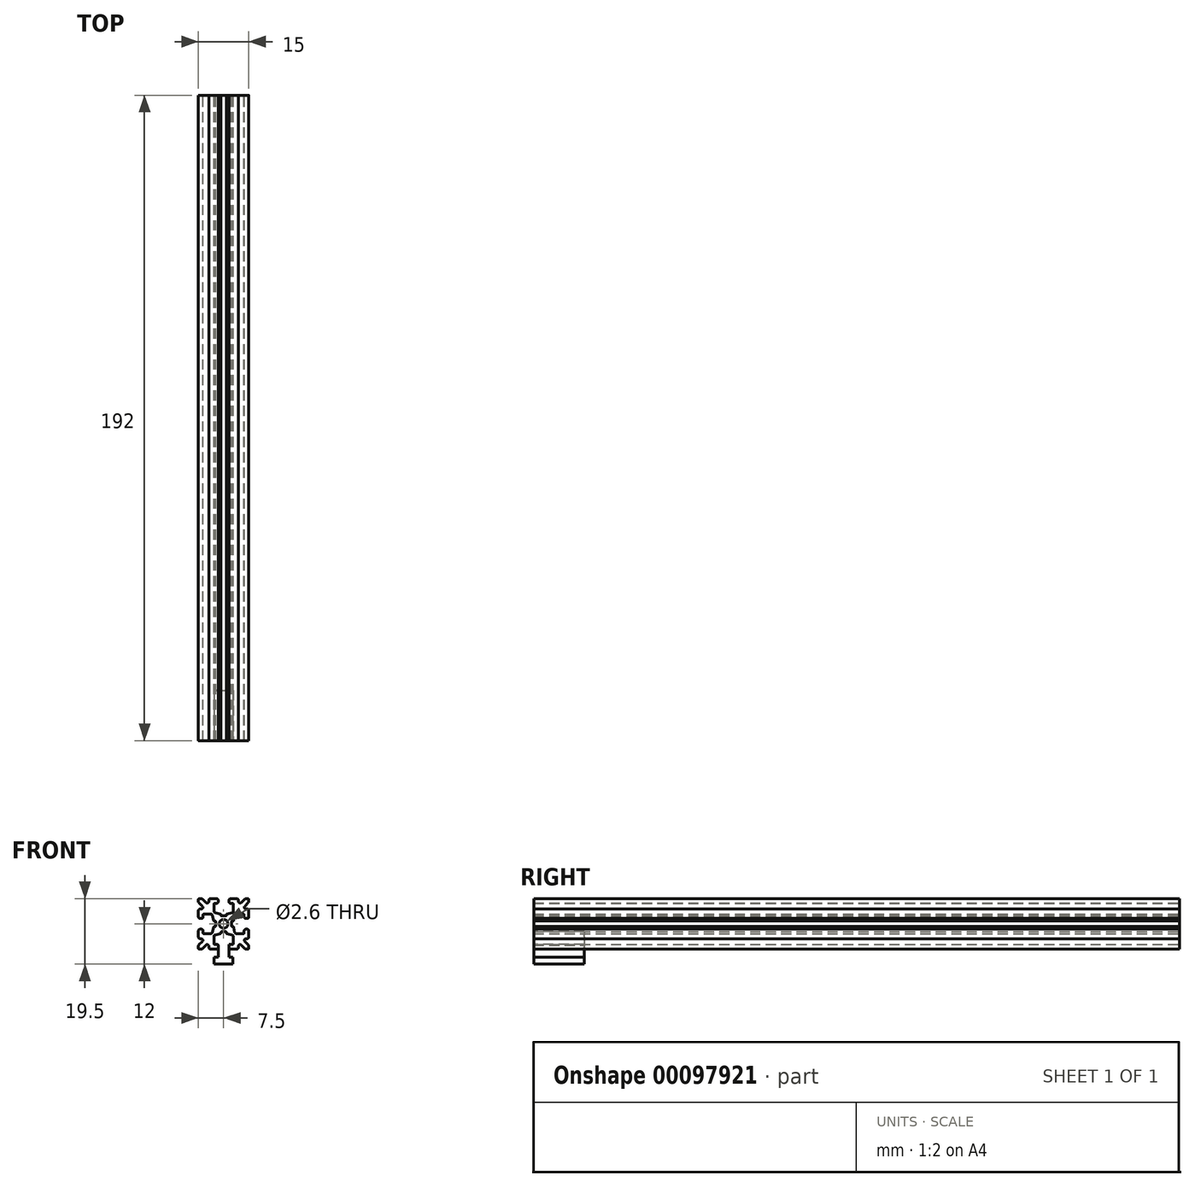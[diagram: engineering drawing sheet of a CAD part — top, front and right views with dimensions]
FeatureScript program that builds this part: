
annotation { "Feature Type Name" : "Feature", "Feature Type Description" : "" }
export const myFeature = defineFeature(function(context is Context, id is Id, definition is map)
    precondition{}
    {
        {
            var Q0;
            Q0=qCreatedBy(makeId("Front.planeOp"),FACE);
            var sketch = newSketch(context, id + "F0", { "sketchPlane" : qUnion([Q0])});
            skLineSegment(sketch, "E0.0.0", {"start": v(0.83, -2.55) * mm, "end": v(0.83, -2.77) * mm});
            skArc(sketch, "E0.0.1", {"start": v(0.83, -2.77) * mm, "mid": v(0.87, -2.9) * mm, "end": v(0.98, -2.97) * mm});
            skLineSegment(sketch, "E0.0.2", {"start": v(0.98, -2.97) * mm, "end": v(2.5, -3.31) * mm});
            skArc(sketch, "E0.0.3", {"start": v(2.5, -3.31) * mm, "mid": v(2.8, -3.49) * mm, "end": v(2.9, -3.8) * mm});
            skLineSegment(sketch, "E0.0.4", {"start": v(2.9, -3.8) * mm, "end": v(2.9, -5.9) * mm});
            skArc(sketch, "E0.0.5", {"start": v(2.9, -5.9) * mm, "mid": v(2.84, -6.04) * mm, "end": v(2.7, -6.1) * mm});
            skLineSegment(sketch, "E0.0.6", {"start": v(2.7, -6.1) * mm, "end": v(2.1, -6.1) * mm});
            skArc(sketch, "E0.0.7", {"start": v(2.1, -6.1) * mm, "mid": v(1.75, -6.25) * mm, "end": v(1.6, -6.6) * mm});
            skLineSegment(sketch, "E0.0.8", {"start": v(1.6, -6.6) * mm, "end": v(1.6, -7) * mm});
            skArc(sketch, "E0.0.9", {"start": v(1.6, -7) * mm, "mid": v(1.75, -7.35) * mm, "end": v(2.1, -7.5) * mm});
            skLineSegment(sketch, "E0.0.10", {"start": v(2.1, -7.5) * mm, "end": v(3.9, -7.5) * mm});
            skArc(sketch, "E0.0.11", {"start": v(3.9, -7.5) * mm, "mid": v(4.25, -7.35) * mm, "end": v(4.4, -7) * mm});
            skLineSegment(sketch, "E0.0.12", {"start": v(4.4, -7) * mm, "end": v(4.4, -6.67) * mm});
            skArc(sketch, "E0.0.13", {"start": v(4.4, -6.67) * mm, "mid": v(4.7, -6.2) * mm, "end": v(5.25, -6.31) * mm});
            skLineSegment(sketch, "E0.0.14", {"start": v(5.25, -6.31) * mm, "end": v(6.3, -7.35) * mm});
            skArc(sketch, "E0.0.15", {"start": v(6.3, -7.35) * mm, "mid": v(6.46, -7.46) * mm, "end": v(6.65, -7.5) * mm});
            skLineSegment(sketch, "E0.0.16", {"start": v(6.65, -7.5) * mm, "end": v(7.25, -7.5) * mm});
            skArc(sketch, "E0.0.17", {"start": v(7.25, -7.5) * mm, "mid": v(7.43, -7.43) * mm, "end": v(7.5, -7.25) * mm});
            skLineSegment(sketch, "E0.0.18", {"start": v(7.5, -7.25) * mm, "end": v(7.5, -6.65) * mm});
            skArc(sketch, "E0.0.19", {"start": v(7.5, -6.65) * mm, "mid": v(7.46, -6.46) * mm, "end": v(7.35, -6.3) * mm});
            skLineSegment(sketch, "E0.0.20", {"start": v(7.35, -6.3) * mm, "end": v(6.31, -5.25) * mm});
            skArc(sketch, "E0.0.21", {"start": v(6.31, -5.25) * mm, "mid": v(6.2, -4.7) * mm, "end": v(6.67, -4.4) * mm});
            skLineSegment(sketch, "E0.0.22", {"start": v(6.67, -4.4) * mm, "end": v(7, -4.4) * mm});
            skArc(sketch, "E0.0.23", {"start": v(7, -4.4) * mm, "mid": v(7.35, -4.25) * mm, "end": v(7.5, -3.9) * mm});
            skLineSegment(sketch, "E0.0.24", {"start": v(7.5, -3.9) * mm, "end": v(7.5, -2.1) * mm});
            skArc(sketch, "E0.0.25", {"start": v(7.5, -2.1) * mm, "mid": v(7.35, -1.75) * mm, "end": v(7, -1.6) * mm});
            skLineSegment(sketch, "E0.0.26", {"start": v(7, -1.6) * mm, "end": v(6.6, -1.6) * mm});
            skArc(sketch, "E0.0.27", {"start": v(6.6, -1.6) * mm, "mid": v(6.25, -1.75) * mm, "end": v(6.1, -2.1) * mm});
            skLineSegment(sketch, "E0.0.28", {"start": v(6.1, -2.1) * mm, "end": v(6.1, -2.7) * mm});
            skArc(sketch, "E0.0.29", {"start": v(6.1, -2.7) * mm, "mid": v(6.04, -2.84) * mm, "end": v(5.9, -2.9) * mm});
            skLineSegment(sketch, "E0.0.30", {"start": v(5.9, -2.9) * mm, "end": v(3.8, -2.9) * mm});
            skArc(sketch, "E0.0.31", {"start": v(3.8, -2.9) * mm, "mid": v(3.49, -2.8) * mm, "end": v(3.31, -2.5) * mm});
            skLineSegment(sketch, "E0.0.32", {"start": v(3.31, -2.5) * mm, "end": v(2.97, -0.98) * mm});
            skArc(sketch, "E0.0.33", {"start": v(2.97, -0.98) * mm, "mid": v(2.9, -0.87) * mm, "end": v(2.77, -0.83) * mm});
            skLineSegment(sketch, "E0.0.34", {"start": v(2.77, -0.83) * mm, "end": v(2.55, -0.83) * mm});
            skArc(sketch, "E0.0.35", {"start": v(2.55, -0.83) * mm, "mid": v(2.4, -0.77) * mm, "end": v(2.35, -0.63) * mm});
            skLineSegment(sketch, "E0.0.36", {"start": v(2.35, -0.63) * mm, "end": v(2.35, 0.63) * mm});
            skArc(sketch, "E0.0.37", {"start": v(2.35, 0.63) * mm, "mid": v(2.4, 0.77) * mm, "end": v(2.55, 0.83) * mm});
            skLineSegment(sketch, "E0.0.38", {"start": v(2.55, 0.83) * mm, "end": v(2.77, 0.83) * mm});
            skArc(sketch, "E0.0.39", {"start": v(2.77, 0.83) * mm, "mid": v(2.9, 0.87) * mm, "end": v(2.97, 0.98) * mm});
            skLineSegment(sketch, "E0.0.40", {"start": v(2.97, 0.98) * mm, "end": v(3.31, 2.5) * mm});
            skArc(sketch, "E0.0.41", {"start": v(3.31, 2.5) * mm, "mid": v(3.49, 2.8) * mm, "end": v(3.8, 2.9) * mm});
            skLineSegment(sketch, "E0.0.42", {"start": v(3.8, 2.9) * mm, "end": v(5.9, 2.9) * mm});
            skArc(sketch, "E0.0.43", {"start": v(5.9, 2.9) * mm, "mid": v(6.04, 2.84) * mm, "end": v(6.1, 2.7) * mm});
            skLineSegment(sketch, "E0.0.44", {"start": v(6.1, 2.7) * mm, "end": v(6.1, 2.1) * mm});
            skArc(sketch, "E0.0.45", {"start": v(6.1, 2.1) * mm, "mid": v(6.25, 1.75) * mm, "end": v(6.6, 1.6) * mm});
            skLineSegment(sketch, "E0.0.46", {"start": v(6.6, 1.6) * mm, "end": v(7, 1.6) * mm});
            skArc(sketch, "E0.0.47", {"start": v(7, 1.6) * mm, "mid": v(7.35, 1.75) * mm, "end": v(7.5, 2.1) * mm});
            skLineSegment(sketch, "E0.0.48", {"start": v(7.5, 2.1) * mm, "end": v(7.5, 3.9) * mm});
            skArc(sketch, "E0.0.49", {"start": v(7.5, 3.9) * mm, "mid": v(7.35, 4.25) * mm, "end": v(7, 4.4) * mm});
            skLineSegment(sketch, "E0.0.50", {"start": v(7, 4.4) * mm, "end": v(6.67, 4.4) * mm});
            skArc(sketch, "E0.0.51", {"start": v(6.67, 4.4) * mm, "mid": v(6.2, 4.7) * mm, "end": v(6.31, 5.25) * mm});
            skLineSegment(sketch, "E0.0.52", {"start": v(6.31, 5.25) * mm, "end": v(7.35, 6.3) * mm});
            skArc(sketch, "E0.0.53", {"start": v(7.35, 6.3) * mm, "mid": v(7.46, 6.46) * mm, "end": v(7.5, 6.65) * mm});
            skLineSegment(sketch, "E0.0.54", {"start": v(7.5, 6.65) * mm, "end": v(7.5, 7.25) * mm});
            skArc(sketch, "E0.0.55", {"start": v(7.5, 7.25) * mm, "mid": v(7.43, 7.43) * mm, "end": v(7.25, 7.5) * mm});
            skLineSegment(sketch, "E0.0.56", {"start": v(7.25, 7.5) * mm, "end": v(6.65, 7.5) * mm});
            skArc(sketch, "E0.0.57", {"start": v(6.65, 7.5) * mm, "mid": v(6.46, 7.46) * mm, "end": v(6.3, 7.35) * mm});
            skLineSegment(sketch, "E0.0.58", {"start": v(6.3, 7.35) * mm, "end": v(5.25, 6.31) * mm});
            skArc(sketch, "E0.0.59", {"start": v(5.25, 6.31) * mm, "mid": v(4.7, 6.2) * mm, "end": v(4.4, 6.67) * mm});
            skLineSegment(sketch, "E0.0.60", {"start": v(4.4, 6.67) * mm, "end": v(4.4, 7) * mm});
            skArc(sketch, "E0.0.61", {"start": v(4.4, 7) * mm, "mid": v(4.25, 7.35) * mm, "end": v(3.9, 7.5) * mm});
            skLineSegment(sketch, "E0.0.62", {"start": v(3.9, 7.5) * mm, "end": v(2.1, 7.5) * mm});
            skArc(sketch, "E0.0.63", {"start": v(2.1, 7.5) * mm, "mid": v(1.75, 7.35) * mm, "end": v(1.6, 7) * mm});
            skLineSegment(sketch, "E0.0.64", {"start": v(1.6, 7) * mm, "end": v(1.6, 6.6) * mm});
            skArc(sketch, "E0.0.65", {"start": v(1.6, 6.6) * mm, "mid": v(1.75, 6.25) * mm, "end": v(2.1, 6.1) * mm});
            skLineSegment(sketch, "E0.0.66", {"start": v(2.1, 6.1) * mm, "end": v(2.7, 6.1) * mm});
            skArc(sketch, "E0.0.67", {"start": v(2.7, 6.1) * mm, "mid": v(2.84, 6.04) * mm, "end": v(2.9, 5.9) * mm});
            skLineSegment(sketch, "E0.0.68", {"start": v(2.9, 5.9) * mm, "end": v(2.9, 3.8) * mm});
            skArc(sketch, "E0.0.69", {"start": v(2.9, 3.8) * mm, "mid": v(2.8, 3.49) * mm, "end": v(2.5, 3.31) * mm});
            skLineSegment(sketch, "E0.0.70", {"start": v(2.5, 3.31) * mm, "end": v(0.98, 2.97) * mm});
            skArc(sketch, "E0.0.71", {"start": v(0.98, 2.97) * mm, "mid": v(0.87, 2.9) * mm, "end": v(0.83, 2.77) * mm});
            skLineSegment(sketch, "E0.0.72", {"start": v(0.83, 2.77) * mm, "end": v(0.83, 2.55) * mm});
            skArc(sketch, "E0.0.73", {"start": v(0.83, 2.55) * mm, "mid": v(0.77, 2.4) * mm, "end": v(0.63, 2.35) * mm});
            skLineSegment(sketch, "E0.0.74", {"start": v(0.63, 2.35) * mm, "end": v(-0.63, 2.35) * mm});
            skArc(sketch, "E0.0.75", {"start": v(-0.63, 2.35) * mm, "mid": v(-0.77, 2.4) * mm, "end": v(-0.83, 2.55) * mm});
            skLineSegment(sketch, "E0.0.76", {"start": v(-0.83, 2.55) * mm, "end": v(-0.83, 2.77) * mm});
            skArc(sketch, "E0.0.77", {"start": v(-0.83, 2.77) * mm, "mid": v(-0.87, 2.9) * mm, "end": v(-0.98, 2.97) * mm});
            skLineSegment(sketch, "E0.0.78", {"start": v(-0.98, 2.97) * mm, "end": v(-2.5, 3.31) * mm});
            skArc(sketch, "E0.0.79", {"start": v(-2.5, 3.31) * mm, "mid": v(-2.8, 3.49) * mm, "end": v(-2.9, 3.8) * mm});
            skLineSegment(sketch, "E0.0.80", {"start": v(-2.9, 3.8) * mm, "end": v(-2.9, 5.9) * mm});
            skArc(sketch, "E0.0.81", {"start": v(-2.9, 5.9) * mm, "mid": v(-2.84, 6.04) * mm, "end": v(-2.7, 6.1) * mm});
            skLineSegment(sketch, "E0.0.82", {"start": v(-2.7, 6.1) * mm, "end": v(-2.1, 6.1) * mm});
            skArc(sketch, "E0.0.83", {"start": v(-2.1, 6.1) * mm, "mid": v(-1.75, 6.25) * mm, "end": v(-1.6, 6.6) * mm});
            skLineSegment(sketch, "E0.0.84", {"start": v(-1.6, 6.6) * mm, "end": v(-1.6, 7) * mm});
            skArc(sketch, "E0.0.85", {"start": v(-1.6, 7) * mm, "mid": v(-1.75, 7.35) * mm, "end": v(-2.1, 7.5) * mm});
            skLineSegment(sketch, "E0.0.86", {"start": v(-2.1, 7.5) * mm, "end": v(-3.9, 7.5) * mm});
            skArc(sketch, "E0.0.87", {"start": v(-3.9, 7.5) * mm, "mid": v(-4.25, 7.35) * mm, "end": v(-4.4, 7) * mm});
            skLineSegment(sketch, "E0.0.88", {"start": v(-4.4, 7) * mm, "end": v(-4.4, 6.67) * mm});
            skArc(sketch, "E0.0.89", {"start": v(-4.4, 6.67) * mm, "mid": v(-4.7, 6.2) * mm, "end": v(-5.25, 6.31) * mm});
            skLineSegment(sketch, "E0.0.90", {"start": v(-5.25, 6.31) * mm, "end": v(-6.3, 7.35) * mm});
            skArc(sketch, "E0.0.91", {"start": v(-6.3, 7.35) * mm, "mid": v(-6.46, 7.46) * mm, "end": v(-6.65, 7.5) * mm});
            skLineSegment(sketch, "E0.0.92", {"start": v(-6.65, 7.5) * mm, "end": v(-7.25, 7.5) * mm});
            skArc(sketch, "E0.0.93", {"start": v(-7.25, 7.5) * mm, "mid": v(-7.43, 7.43) * mm, "end": v(-7.5, 7.25) * mm});
            skLineSegment(sketch, "E0.0.94", {"start": v(-7.5, 7.25) * mm, "end": v(-7.5, 6.65) * mm});
            skArc(sketch, "E0.0.95", {"start": v(-7.5, 6.65) * mm, "mid": v(-7.46, 6.46) * mm, "end": v(-7.35, 6.3) * mm});
            skLineSegment(sketch, "E0.0.96", {"start": v(-7.35, 6.3) * mm, "end": v(-6.31, 5.25) * mm});
            skArc(sketch, "E0.0.97", {"start": v(-6.31, 5.25) * mm, "mid": v(-6.2, 4.7) * mm, "end": v(-6.67, 4.4) * mm});
            skLineSegment(sketch, "E0.0.98", {"start": v(-6.67, 4.4) * mm, "end": v(-7, 4.4) * mm});
            skArc(sketch, "E0.0.99", {"start": v(-7, 4.4) * mm, "mid": v(-7.35, 4.25) * mm, "end": v(-7.5, 3.9) * mm});
            skLineSegment(sketch, "E0.0.100", {"start": v(-7.5, 3.9) * mm, "end": v(-7.5, 2.1) * mm});
            skArc(sketch, "E0.0.101", {"start": v(-7.5, 2.1) * mm, "mid": v(-7.35, 1.75) * mm, "end": v(-7, 1.6) * mm});
            skLineSegment(sketch, "E0.0.102", {"start": v(-7, 1.6) * mm, "end": v(-6.6, 1.6) * mm});
            skArc(sketch, "E0.0.103", {"start": v(-6.6, 1.6) * mm, "mid": v(-6.25, 1.75) * mm, "end": v(-6.1, 2.1) * mm});
            skLineSegment(sketch, "E0.0.104", {"start": v(-6.1, 2.1) * mm, "end": v(-6.1, 2.7) * mm});
            skArc(sketch, "E0.0.105", {"start": v(-6.1, 2.7) * mm, "mid": v(-6.04, 2.84) * mm, "end": v(-5.9, 2.9) * mm});
            skLineSegment(sketch, "E0.0.106", {"start": v(-5.9, 2.9) * mm, "end": v(-3.8, 2.9) * mm});
            skArc(sketch, "E0.0.107", {"start": v(-3.8, 2.9) * mm, "mid": v(-3.49, 2.8) * mm, "end": v(-3.31, 2.5) * mm});
            skLineSegment(sketch, "E0.0.108", {"start": v(-3.31, 2.5) * mm, "end": v(-2.97, 0.98) * mm});
            skArc(sketch, "E0.0.109", {"start": v(-2.97, 0.98) * mm, "mid": v(-2.9, 0.87) * mm, "end": v(-2.77, 0.83) * mm});
            skLineSegment(sketch, "E0.0.110", {"start": v(-2.77, 0.83) * mm, "end": v(-2.55, 0.83) * mm});
            skArc(sketch, "E0.0.111", {"start": v(-2.55, 0.83) * mm, "mid": v(-2.4, 0.77) * mm, "end": v(-2.35, 0.63) * mm});
            skLineSegment(sketch, "E0.0.112", {"start": v(-2.35, 0.63) * mm, "end": v(-2.35, -0.63) * mm});
            skArc(sketch, "E0.0.113", {"start": v(-2.35, -0.63) * mm, "mid": v(-2.4, -0.77) * mm, "end": v(-2.55, -0.83) * mm});
            skLineSegment(sketch, "E0.0.114", {"start": v(-2.55, -0.83) * mm, "end": v(-2.77, -0.83) * mm});
            skArc(sketch, "E0.0.115", {"start": v(-2.77, -0.83) * mm, "mid": v(-2.9, -0.87) * mm, "end": v(-2.97, -0.98) * mm});
            skLineSegment(sketch, "E0.0.116", {"start": v(-2.97, -0.98) * mm, "end": v(-3.31, -2.5) * mm});
            skArc(sketch, "E0.0.117", {"start": v(-3.31, -2.5) * mm, "mid": v(-3.49, -2.8) * mm, "end": v(-3.8, -2.9) * mm});
            skLineSegment(sketch, "E0.0.118", {"start": v(-3.8, -2.9) * mm, "end": v(-5.9, -2.9) * mm});
            skArc(sketch, "E0.0.119", {"start": v(-5.9, -2.9) * mm, "mid": v(-6.04, -2.84) * mm, "end": v(-6.1, -2.7) * mm});
            skLineSegment(sketch, "E0.0.120", {"start": v(-6.1, -2.7) * mm, "end": v(-6.1, -2.1) * mm});
            skArc(sketch, "E0.0.121", {"start": v(-6.1, -2.1) * mm, "mid": v(-6.25, -1.75) * mm, "end": v(-6.6, -1.6) * mm});
            skLineSegment(sketch, "E0.0.122", {"start": v(-6.6, -1.6) * mm, "end": v(-7, -1.6) * mm});
            skArc(sketch, "E0.0.123", {"start": v(-7, -1.6) * mm, "mid": v(-7.35, -1.75) * mm, "end": v(-7.5, -2.1) * mm});
            skLineSegment(sketch, "E0.0.124", {"start": v(-7.5, -2.1) * mm, "end": v(-7.5, -3.9) * mm});
            skArc(sketch, "E0.0.125", {"start": v(-7.5, -3.9) * mm, "mid": v(-7.35, -4.25) * mm, "end": v(-7, -4.4) * mm});
            skLineSegment(sketch, "E0.0.126", {"start": v(-7, -4.4) * mm, "end": v(-6.67, -4.4) * mm});
            skArc(sketch, "E0.0.127", {"start": v(-6.67, -4.4) * mm, "mid": v(-6.2, -4.7) * mm, "end": v(-6.31, -5.25) * mm});
            skLineSegment(sketch, "E0.0.128", {"start": v(-6.31, -5.25) * mm, "end": v(-7.35, -6.3) * mm});
            skArc(sketch, "E0.0.129", {"start": v(-7.35, -6.3) * mm, "mid": v(-7.46, -6.46) * mm, "end": v(-7.5, -6.65) * mm});
            skLineSegment(sketch, "E0.0.130", {"start": v(-7.5, -6.65) * mm, "end": v(-7.5, -7.25) * mm});
            skArc(sketch, "E0.0.131", {"start": v(-7.5, -7.25) * mm, "mid": v(-7.43, -7.43) * mm, "end": v(-7.25, -7.5) * mm});
            skLineSegment(sketch, "E0.0.132", {"start": v(-7.25, -7.5) * mm, "end": v(-6.65, -7.5) * mm});
            skArc(sketch, "E0.0.133", {"start": v(-6.65, -7.5) * mm, "mid": v(-6.46, -7.46) * mm, "end": v(-6.3, -7.35) * mm});
            skLineSegment(sketch, "E0.0.134", {"start": v(-6.3, -7.35) * mm, "end": v(-5.25, -6.31) * mm});
            skArc(sketch, "E0.0.135", {"start": v(-5.25, -6.31) * mm, "mid": v(-4.7, -6.2) * mm, "end": v(-4.4, -6.67) * mm});
            skLineSegment(sketch, "E0.0.136", {"start": v(-4.4, -6.67) * mm, "end": v(-4.4, -7) * mm});
            skArc(sketch, "E0.0.137", {"start": v(-4.4, -7) * mm, "mid": v(-4.25, -7.35) * mm, "end": v(-3.9, -7.5) * mm});
            skLineSegment(sketch, "E0.0.138", {"start": v(-3.9, -7.5) * mm, "end": v(-2.1, -7.5) * mm});
            skArc(sketch, "E0.0.139", {"start": v(-2.1, -7.5) * mm, "mid": v(-1.75, -7.35) * mm, "end": v(-1.6, -7) * mm});
            skLineSegment(sketch, "E0.0.140", {"start": v(-1.6, -7) * mm, "end": v(-1.6, -6.6) * mm});
            skArc(sketch, "E0.0.141", {"start": v(-1.6, -6.6) * mm, "mid": v(-1.75, -6.25) * mm, "end": v(-2.1, -6.1) * mm});
            skLineSegment(sketch, "E0.0.142", {"start": v(-2.1, -6.1) * mm, "end": v(-2.7, -6.1) * mm});
            skArc(sketch, "E0.0.143", {"start": v(-2.7, -6.1) * mm, "mid": v(-2.84, -6.04) * mm, "end": v(-2.9, -5.9) * mm});
            skLineSegment(sketch, "E0.0.144", {"start": v(-2.9, -5.9) * mm, "end": v(-2.9, -3.8) * mm});
            skArc(sketch, "E0.0.145", {"start": v(-2.9, -3.8) * mm, "mid": v(-2.8, -3.49) * mm, "end": v(-2.5, -3.31) * mm});
            skLineSegment(sketch, "E0.0.146", {"start": v(-2.5, -3.31) * mm, "end": v(-0.98, -2.97) * mm});
            skArc(sketch, "E0.0.147", {"start": v(-0.98, -2.97) * mm, "mid": v(-0.87, -2.9) * mm, "end": v(-0.83, -2.77) * mm});
            skLineSegment(sketch, "E0.0.148", {"start": v(-0.83, -2.77) * mm, "end": v(-0.83, -2.55) * mm});
            skArc(sketch, "E0.0.149", {"start": v(-0.83, -2.55) * mm, "mid": v(-0.77, -2.4) * mm, "end": v(-0.63, -2.35) * mm});
            skLineSegment(sketch, "E0.0.150", {"start": v(-0.63, -2.35) * mm, "end": v(0.63, -2.35) * mm});
            skArc(sketch, "E0.0.151", {"start": v(0.63, -2.35) * mm, "mid": v(0.77, -2.4) * mm, "end": v(0.83, -2.55) * mm});
            skPoint(sketch, "E1", {"position": v(0, 0) * mm});
            skPoint(sketch, "E1.positionSnap0", {"position": v(0, 2.35) * mm});
            skPoint(sketch, "E1.positionSnap1", {"position": v(2.35, 0) * mm});
            skCircle(sketch, "E2", {"center": v(0, 0) * mm, "radius": 1.3 * mm});
            skSolve(sketch);
        }
        {
            var Q0;
            Q0=makeQuery(id+"F0.imprint","IMPRINT",FACE,{"disambiguationData":[TD([[makeQuery(id+"F0.imprint","IMPRINT",EDGE,{"derivedFrom":sQuery(id+"F0.wireOp",EDGE,"E0.0.0")}),1.0]])]});
            extrude(context, id + "F1", {"entities" : qUnion([Q0]), "endBound" : BoundingType.SYMMETRIC, "depth" : 192 * mm});
        }
        {
            var Q0;
            Q0=makeQuery(id+"F1.opExtrude","CAP_FACE",FACE,{"disambiguationData":[OSD([sQuery(id+"F0.wireOp",EDGE,"E0.0.0"),sQuery(id+"F0.wireOp",EDGE,"E0.0.1"),sQuery(id+"F0.wireOp",EDGE,"E0.0.2"),sQuery(id+"F0.wireOp",EDGE,"E0.0.3"),sQuery(id+"F0.wireOp",EDGE,"E0.0.4"),sQuery(id+"F0.wireOp",EDGE,"E0.0.5"),sQuery(id+"F0.wireOp",EDGE,"E0.0.6"),sQuery(id+"F0.wireOp",EDGE,"E0.0.7"),sQuery(id+"F0.wireOp",EDGE,"E0.0.8"),sQuery(id+"F0.wireOp",EDGE,"E0.0.9"),sQuery(id+"F0.wireOp",EDGE,"E0.0.10"),sQuery(id+"F0.wireOp",EDGE,"E0.0.11"),sQuery(id+"F0.wireOp",EDGE,"E0.0.12"),sQuery(id+"F0.wireOp",EDGE,"E0.0.13"),sQuery(id+"F0.wireOp",EDGE,"E0.0.14"),sQuery(id+"F0.wireOp",EDGE,"E0.0.15"),sQuery(id+"F0.wireOp",EDGE,"E0.0.16"),sQuery(id+"F0.wireOp",EDGE,"E0.0.17"),sQuery(id+"F0.wireOp",EDGE,"E0.0.18"),sQuery(id+"F0.wireOp",EDGE,"E0.0.19"),sQuery(id+"F0.wireOp",EDGE,"E0.0.20"),sQuery(id+"F0.wireOp",EDGE,"E0.0.21"),sQuery(id+"F0.wireOp",EDGE,"E0.0.22"),sQuery(id+"F0.wireOp",EDGE,"E0.0.23"),sQuery(id+"F0.wireOp",EDGE,"E0.0.24"),sQuery(id+"F0.wireOp",EDGE,"E0.0.25"),sQuery(id+"F0.wireOp",EDGE,"E0.0.26"),sQuery(id+"F0.wireOp",EDGE,"E0.0.27"),sQuery(id+"F0.wireOp",EDGE,"E0.0.28"),sQuery(id+"F0.wireOp",EDGE,"E0.0.29"),sQuery(id+"F0.wireOp",EDGE,"E0.0.30"),sQuery(id+"F0.wireOp",EDGE,"E0.0.31"),sQuery(id+"F0.wireOp",EDGE,"E0.0.32"),sQuery(id+"F0.wireOp",EDGE,"E0.0.33"),sQuery(id+"F0.wireOp",EDGE,"E0.0.34"),sQuery(id+"F0.wireOp",EDGE,"E0.0.35"),sQuery(id+"F0.wireOp",EDGE,"E0.0.36"),sQuery(id+"F0.wireOp",EDGE,"E0.0.37"),sQuery(id+"F0.wireOp",EDGE,"E0.0.38"),sQuery(id+"F0.wireOp",EDGE,"E0.0.39"),sQuery(id+"F0.wireOp",EDGE,"E0.0.40"),sQuery(id+"F0.wireOp",EDGE,"E0.0.41"),sQuery(id+"F0.wireOp",EDGE,"E0.0.42"),sQuery(id+"F0.wireOp",EDGE,"E0.0.43"),sQuery(id+"F0.wireOp",EDGE,"E0.0.44"),sQuery(id+"F0.wireOp",EDGE,"E0.0.45"),sQuery(id+"F0.wireOp",EDGE,"E0.0.46"),sQuery(id+"F0.wireOp",EDGE,"E0.0.47"),sQuery(id+"F0.wireOp",EDGE,"E0.0.48"),sQuery(id+"F0.wireOp",EDGE,"E0.0.49"),sQuery(id+"F0.wireOp",EDGE,"E0.0.50"),sQuery(id+"F0.wireOp",EDGE,"E0.0.51"),sQuery(id+"F0.wireOp",EDGE,"E0.0.52"),sQuery(id+"F0.wireOp",EDGE,"E0.0.53"),sQuery(id+"F0.wireOp",EDGE,"E0.0.54"),sQuery(id+"F0.wireOp",EDGE,"E0.0.55"),sQuery(id+"F0.wireOp",EDGE,"E0.0.56"),sQuery(id+"F0.wireOp",EDGE,"E0.0.57"),sQuery(id+"F0.wireOp",EDGE,"E0.0.58"),sQuery(id+"F0.wireOp",EDGE,"E0.0.59"),sQuery(id+"F0.wireOp",EDGE,"E0.0.60"),sQuery(id+"F0.wireOp",EDGE,"E0.0.61"),sQuery(id+"F0.wireOp",EDGE,"E0.0.62"),sQuery(id+"F0.wireOp",EDGE,"E0.0.63"),sQuery(id+"F0.wireOp",EDGE,"E0.0.64"),sQuery(id+"F0.wireOp",EDGE,"E0.0.65"),sQuery(id+"F0.wireOp",EDGE,"E0.0.66"),sQuery(id+"F0.wireOp",EDGE,"E0.0.67"),sQuery(id+"F0.wireOp",EDGE,"E0.0.68"),sQuery(id+"F0.wireOp",EDGE,"E0.0.69"),sQuery(id+"F0.wireOp",EDGE,"E0.0.70"),sQuery(id+"F0.wireOp",EDGE,"E0.0.71"),sQuery(id+"F0.wireOp",EDGE,"E0.0.72"),sQuery(id+"F0.wireOp",EDGE,"E0.0.73"),sQuery(id+"F0.wireOp",EDGE,"E0.0.74"),sQuery(id+"F0.wireOp",EDGE,"E0.0.75"),sQuery(id+"F0.wireOp",EDGE,"E0.0.76"),sQuery(id+"F0.wireOp",EDGE,"E0.0.77"),sQuery(id+"F0.wireOp",EDGE,"E0.0.78"),sQuery(id+"F0.wireOp",EDGE,"E0.0.79"),sQuery(id+"F0.wireOp",EDGE,"E0.0.80"),sQuery(id+"F0.wireOp",EDGE,"E0.0.81"),sQuery(id+"F0.wireOp",EDGE,"E0.0.82"),sQuery(id+"F0.wireOp",EDGE,"E0.0.83"),sQuery(id+"F0.wireOp",EDGE,"E0.0.84"),sQuery(id+"F0.wireOp",EDGE,"E0.0.85"),sQuery(id+"F0.wireOp",EDGE,"E0.0.86"),sQuery(id+"F0.wireOp",EDGE,"E0.0.87"),sQuery(id+"F0.wireOp",EDGE,"E0.0.88"),sQuery(id+"F0.wireOp",EDGE,"E0.0.89"),sQuery(id+"F0.wireOp",EDGE,"E0.0.90"),sQuery(id+"F0.wireOp",EDGE,"E0.0.91"),sQuery(id+"F0.wireOp",EDGE,"E0.0.92"),sQuery(id+"F0.wireOp",EDGE,"E0.0.93"),sQuery(id+"F0.wireOp",EDGE,"E0.0.94"),sQuery(id+"F0.wireOp",EDGE,"E0.0.95"),sQuery(id+"F0.wireOp",EDGE,"E0.0.96"),sQuery(id+"F0.wireOp",EDGE,"E0.0.97"),sQuery(id+"F0.wireOp",EDGE,"E0.0.98"),sQuery(id+"F0.wireOp",EDGE,"E0.0.99"),sQuery(id+"F0.wireOp",EDGE,"E0.0.100"),sQuery(id+"F0.wireOp",EDGE,"E0.0.101"),sQuery(id+"F0.wireOp",EDGE,"E0.0.102"),sQuery(id+"F0.wireOp",EDGE,"E0.0.103"),sQuery(id+"F0.wireOp",EDGE,"E0.0.104"),sQuery(id+"F0.wireOp",EDGE,"E0.0.105"),sQuery(id+"F0.wireOp",EDGE,"E0.0.106"),sQuery(id+"F0.wireOp",EDGE,"E0.0.107"),sQuery(id+"F0.wireOp",EDGE,"E0.0.108"),sQuery(id+"F0.wireOp",EDGE,"E0.0.109"),sQuery(id+"F0.wireOp",EDGE,"E0.0.110"),sQuery(id+"F0.wireOp",EDGE,"E0.0.111"),sQuery(id+"F0.wireOp",EDGE,"E0.0.112"),sQuery(id+"F0.wireOp",EDGE,"E0.0.113"),sQuery(id+"F0.wireOp",EDGE,"E0.0.114"),sQuery(id+"F0.wireOp",EDGE,"E0.0.115"),sQuery(id+"F0.wireOp",EDGE,"E0.0.116"),sQuery(id+"F0.wireOp",EDGE,"E0.0.117"),sQuery(id+"F0.wireOp",EDGE,"E0.0.118"),sQuery(id+"F0.wireOp",EDGE,"E0.0.119"),sQuery(id+"F0.wireOp",EDGE,"E0.0.120"),sQuery(id+"F0.wireOp",EDGE,"E0.0.121"),sQuery(id+"F0.wireOp",EDGE,"E0.0.122"),sQuery(id+"F0.wireOp",EDGE,"E0.0.123"),sQuery(id+"F0.wireOp",EDGE,"E0.0.124"),sQuery(id+"F0.wireOp",EDGE,"E0.0.125"),sQuery(id+"F0.wireOp",EDGE,"E0.0.126"),sQuery(id+"F0.wireOp",EDGE,"E0.0.127"),sQuery(id+"F0.wireOp",EDGE,"E0.0.128"),sQuery(id+"F0.wireOp",EDGE,"E0.0.129"),sQuery(id+"F0.wireOp",EDGE,"E0.0.130"),sQuery(id+"F0.wireOp",EDGE,"E0.0.131"),sQuery(id+"F0.wireOp",EDGE,"E0.0.132"),sQuery(id+"F0.wireOp",EDGE,"E0.0.133"),sQuery(id+"F0.wireOp",EDGE,"E0.0.134"),sQuery(id+"F0.wireOp",EDGE,"E0.0.135"),sQuery(id+"F0.wireOp",EDGE,"E0.0.136"),sQuery(id+"F0.wireOp",EDGE,"E0.0.137"),sQuery(id+"F0.wireOp",EDGE,"E0.0.138"),sQuery(id+"F0.wireOp",EDGE,"E0.0.139"),sQuery(id+"F0.wireOp",EDGE,"E0.0.140"),sQuery(id+"F0.wireOp",EDGE,"E0.0.141"),sQuery(id+"F0.wireOp",EDGE,"E0.0.142"),sQuery(id+"F0.wireOp",EDGE,"E0.0.143"),sQuery(id+"F0.wireOp",EDGE,"E0.0.144"),sQuery(id+"F0.wireOp",EDGE,"E0.0.145"),sQuery(id+"F0.wireOp",EDGE,"E0.0.146"),sQuery(id+"F0.wireOp",EDGE,"E0.0.147"),sQuery(id+"F0.wireOp",EDGE,"E0.0.148"),sQuery(id+"F0.wireOp",EDGE,"E0.0.149"),sQuery(id+"F0.wireOp",EDGE,"E0.0.150"),sQuery(id+"F0.wireOp",EDGE,"E0.0.151"),sQuery(id+"F0.wireOp",EDGE,"E2")])],"isStart":false});
            var sketch = newSketch(context, id + "F2", { "sketchPlane" : qUnion([Q0])});
            skLineSegment(sketch, "E3", {"start": v(-1.6, -8) * mm, "end": v(-1.6, -6.1) * mm});
            skLineSegment(sketch, "E4", {"start": v(-1.6, -6.1) * mm, "end": v(-2.8, -6.1) * mm});
            skLineSegment(sketch, "E5.0", {"start": v(-2.8, -6.1) * mm, "end": v(-2.8, -4) * mm});
            skLineSegment(sketch, "E6.0", {"start": v(-2.8, -4) * mm, "end": v(0, -4) * mm});
            skLineSegment(sketch, "E7", {"start": v(-1.6, -8) * mm, "end": v(0, -8) * mm, "construction": true});
            skLineSegment(sketch, "E8", {"start": v(0, -8) * mm, "end": v(0, -4) * mm, "construction": true});
            skLineSegment(sketch, "E9.MirrorCS", {"start": v(-2.8, -12) * mm, "end": v(0, -12) * mm});
            skLineSegment(sketch, "E10.MirrorCS", {"start": v(-1.6, -9.9) * mm, "end": v(-2.8, -9.9) * mm});
            skLineSegment(sketch, "E11.MirrorCS", {"start": v(-2.8, -9.9) * mm, "end": v(-2.8, -12) * mm});
            skLineSegment(sketch, "E12.MirrorCS", {"start": v(-1.6, -8) * mm, "end": v(-1.6, -9.9) * mm});
            skLineSegment(sketch, "E13.MirrorCS", {"start": v(0, -8) * mm, "end": v(0, -12) * mm, "construction": true});
            skLineSegment(sketch, "E14.MirrorCS", {"start": v(2.8, -4) * mm, "end": v(0, -4) * mm});
            skLineSegment(sketch, "E15.MirrorCS", {"start": v(2.8, -6.1) * mm, "end": v(2.8, -4) * mm});
            skLineSegment(sketch, "E16.MirrorCS", {"start": v(2.8, -9.9) * mm, "end": v(2.8, -12) * mm});
            skLineSegment(sketch, "E17.MirrorCS", {"start": v(1.6, -6.1) * mm, "end": v(2.8, -6.1) * mm});
            skLineSegment(sketch, "E18.MirrorCS", {"start": v(1.6, -8) * mm, "end": v(1.6, -6.1) * mm});
            skLineSegment(sketch, "E19.MirrorCS", {"start": v(1.6, -9.9) * mm, "end": v(2.8, -9.9) * mm});
            skLineSegment(sketch, "E20.MirrorCS", {"start": v(2.8, -12) * mm, "end": v(0, -12) * mm});
            skLineSegment(sketch, "E21.MirrorCS", {"start": v(1.6, -8) * mm, "end": v(1.6, -9.9) * mm});
            skSolve(sketch);
        }
        {
            var Q0;
            {var subQ15=sQuery(id+"F2.wireOp",EDGE,"DLqnf9M1-cb26-jMbR-sq29-XcbJybY2cm9H");Q0=makeQuery(id+"F2.imprint","IMPRINT",FACE,{"disambiguationData":[TD([[makeQuery(id+"F2.imprint","IMPRINT",EDGE,{"derivedFrom":subQ15}),-1.0]])]});}
            var Q1;
            {var subQ1=makeQuery(id+"F1.opExtrude","CAP_EDGE",EDGE,{"disambiguationData":[OSD([sQuery(id+"F0.wireOp",EDGE,"E0.0.5")])],"isStart":false});Q1=makeQuery(id+"F2.imprint","IMPRINT",FACE,{"disambiguationData":[TD([[makeQuery(id+"F2.imprint","IMPRINT",EDGE,{"derivedFrom":subQ1}),1.0]])]});}
            var Q2;
            {var subQ1=makeQuery(id+"F1.opExtrude","CAP_EDGE",EDGE,{"disambiguationData":[OSD([sQuery(id+"F0.wireOp",EDGE,"E0.0.143")])],"isStart":false});Q2=makeQuery(id+"F2.imprint","IMPRINT",FACE,{"disambiguationData":[TD([[makeQuery(id+"F2.imprint","IMPRINT",EDGE,{"derivedFrom":subQ1}),1.0]])]});}
            var Q3;
            {var subQ11=sQuery(id+"F2.wireOp",EDGE,"E6.0");Q3=makeQuery(id+"F2.imprint","IMPRINT",FACE,{"disambiguationData":[TD([[makeQuery(id+"F2.imprint","IMPRINT",EDGE,{"derivedFrom":subQ11}),-1.0]])]});}
            extrude(context, id + "F3", {"entities" : qUnion([Q0, Q1, Q2, Q3]), "oppositeDirection" : true, "depth" : 15 * mm});
        }
        {
            var Q0;
            Q0=makeQuery(id+"F3.opExtrude","SWEPT_EDGE",EDGE,{"disambiguationData":[OSD([sQuery(id+"F2.wireOp",EDGE,"E4"),sQuery(id+"F2.wireOp",EDGE,"JMUfWz5n-XeYh-gAeM-SpF9-6zzdlZEgvJd6")])]});
            var Q1;
            Q1=makeQuery(id+"F3.opExtrude","SWEPT_EDGE",EDGE,{"disambiguationData":[OSD([sQuery(id+"F2.wireOp",EDGE,"8ITzd27P-ogiu-v4g7-8rLW-PKKwLHGkHbPP"),sQuery(id+"F2.wireOp",EDGE,"WMcWWASD-56yT-hrbX-fbI3-SrIpCFeLDnTT")])]});
            var Q2;
            Q2=makeQuery(id+"F3.opExtrude","SWEPT_EDGE",EDGE,{"disambiguationData":[OSD([sQuery(id+"F0.wireOp",EDGE,"E0.0.145"),sQuery(id+"F2.wireOp",EDGE,"DLqnf9M1-cb26-jMbR-sq29-XcbJybY2cm9H"),sQuery(id+"F2.wireOp",EDGE,"JMUfWz5n-XeYh-gAeM-SpF9-6zzdlZEgvJd6")])]});
            var Q3;
            Q3=makeQuery(id+"F3.opExtrude","SWEPT_EDGE",EDGE,{"disambiguationData":[OSD([sQuery(id+"F0.wireOp",EDGE,"E0.0.3"),sQuery(id+"F2.wireOp",EDGE,"DLqnf9M1-cb26-jMbR-sq29-XcbJybY2cm9H"),sQuery(id+"F2.wireOp",EDGE,"8ITzd27P-ogiu-v4g7-8rLW-PKKwLHGkHbPP")])]});
            var Q4;
            Q4=makeQuery(id+"F3.opExtrude","SWEPT_EDGE",EDGE,{"disambiguationData":[OSD([sQuery(id+"F2.wireOp",EDGE,"089dc7a1-2ac2-4524-9453-b4d9188fe5ce5.MirrorCS"),sQuery(id+"F2.wireOp",EDGE,"089dc7a1-2ac2-4524-9453-b4d9188fe5ce6.MirrorCS")])]});
            var Q5;
            Q5=makeQuery(id+"F3.opExtrude","SWEPT_EDGE",EDGE,{"disambiguationData":[OSD([sQuery(id+"F2.wireOp",EDGE,"089dc7a1-2ac2-4524-9453-b4d9188fe5ce2.MirrorCS"),sQuery(id+"F2.wireOp",EDGE,"089dc7a1-2ac2-4524-9453-b4d9188fe5ce6.MirrorCS")])]});
            var Q6;
            Q6=makeQuery(id+"F3.opExtrude","SWEPT_EDGE",EDGE,{"disambiguationData":[OSD([sQuery(id+"F2.wireOp",EDGE,"089dc7a1-2ac2-4524-9453-b4d9188fe5ce4.MirrorCS"),sQuery(id+"F2.wireOp",EDGE,"089dc7a1-2ac2-4524-9453-b4d9188fe5ce5.MirrorCS")])]});
            var Q7;
            Q7=makeQuery(id+"F3.opExtrude","SWEPT_EDGE",EDGE,{"disambiguationData":[OSD([sQuery(id+"F2.wireOp",EDGE,"089dc7a1-2ac2-4524-9453-b4d9188fe5ce0.MirrorCS"),sQuery(id+"F2.wireOp",EDGE,"089dc7a1-2ac2-4524-9453-b4d9188fe5ce2.MirrorCS")])]});
            chamfer(context, id + "F4", {"entities" : qUnion([Q0, Q1, Q2, Q3, Q4, Q5, Q6, Q7]), "width" : 0.25 * mm, "tangentPropagation" : true});
        }
    });
